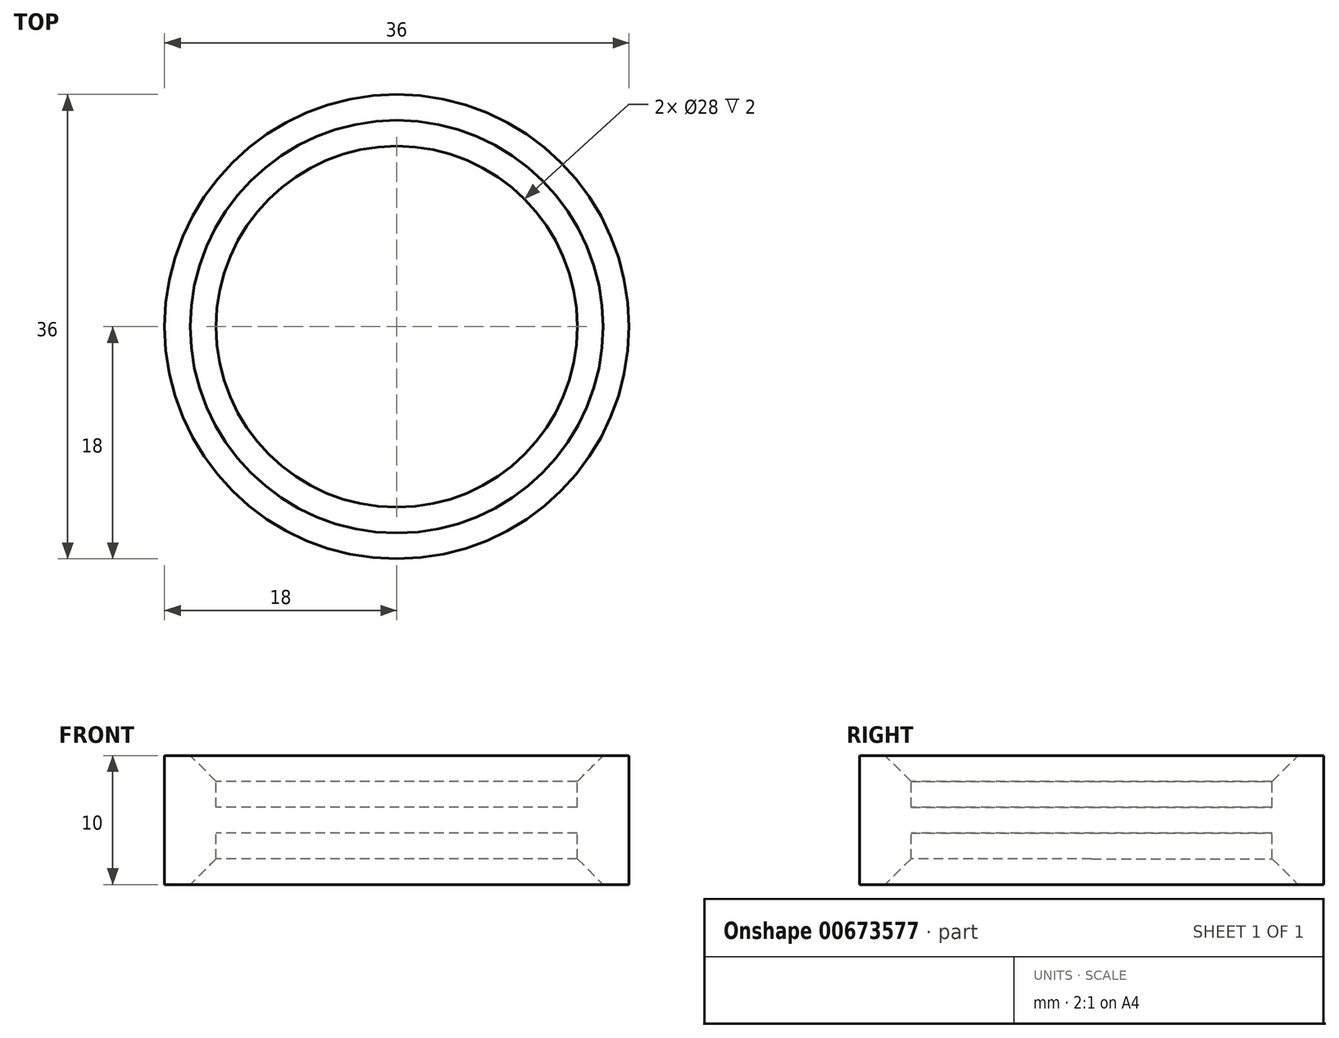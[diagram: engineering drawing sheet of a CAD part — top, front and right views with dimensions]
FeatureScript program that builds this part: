
annotation { "Feature Type Name" : "Feature", "Feature Type Description" : "" }
export const myFeature = defineFeature(function(context is Context, id is Id, definition is map)
    precondition{}
    {
        {
            var Q0;
            Q0=qCreatedBy(makeId("Right.planeOp"),FACE);
            var sketch = newSketch(context, id + "F0", { "sketchPlane" : qUnion([Q0])});
            skLineSegment(sketch, "E0", {"start": v(0, 15.84) * mm, "end": v(0, -19.11) * mm, "construction": true});
            skLineSegment(sketch, "E1", {"start": v(-18, 1.96) * mm, "end": v(-18, -8.04) * mm});
            skLineSegment(sketch, "E2", {"start": v(-18, -8.04) * mm, "end": v(-14, -8.04) * mm});
            skLineSegment(sketch, "E3", {"start": v(-14, -8.04) * mm, "end": v(-14, -4.04) * mm});
            skLineSegment(sketch, "E4", {"start": v(-14, -4.04) * mm, "end": v(0, -4.04) * mm});
            skLineSegment(sketch, "E5", {"start": v(0, -4.04) * mm, "end": v(0, -2.04) * mm});
            skLineSegment(sketch, "E6", {"start": v(0, -2.04) * mm, "end": v(-14, -2.04) * mm});
            skLineSegment(sketch, "E7", {"start": v(-14, -2.04) * mm, "end": v(-14, 1.96) * mm});
            skLineSegment(sketch, "E8", {"start": v(-14, 1.96) * mm, "end": v(-18, 1.96) * mm});
            skSolve(sketch);
        }
        {
            var Q0;
            Q0=makeQuery(id+"F0.imprint","IMPRINT",FACE,{"disambiguationData":[TD([[makeQuery(id+"F0.imprint","IMPRINT",EDGE,{"derivedFrom":sQuery(id+"F0.wireOp",EDGE,"E1")}),1.0]])]});
            var Q1;
            Q1=sQuery(id+"F0.wireOp",EDGE,"E0");
            revolve(context, id + "F1", {"entities" : qUnion([Q0]), "axis" : qUnion([Q1]), "revolveType" : RevolveType.FULL});
        }
        {
            var Q0;
            Q0=makeQuery(id+"F1.opRevolve","SWEPT_EDGE",EDGE,{"disambiguationData":[OSD([sQuery(id+"F0.wireOp",EDGE,"E7"),sQuery(id+"F0.wireOp",EDGE,"E8")])]});
            var Q1;
            Q1=makeQuery(id+"F1.opRevolve","SWEPT_EDGE",EDGE,{"disambiguationData":[OSD([sQuery(id+"F0.wireOp",EDGE,"E2"),sQuery(id+"F0.wireOp",EDGE,"E3")])]});
            chamfer(context, id + "F2", {"entities" : qUnion([Q0, Q1]), "width" : 2 * mm, "tangentPropagation" : true});
        }
    });
